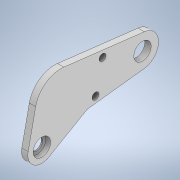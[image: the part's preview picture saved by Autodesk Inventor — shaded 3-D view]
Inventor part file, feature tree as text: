
AUTODESK INVENTOR PART (.ipt)
format: ipt  version: 2020 (Build 240168000, 168)  size: 390,656 bytes
history: native  units: mm
features: extrude x7, sketch x4, projected_geometry x3
ambient origin geometry x8: Origin, YZ Plane, XZ Plane, XY Plane, X Axis, Y Axis, Z Axis, Center Point
bodies: Body1 (feature_tree)
feature tree (14):
  extrude  "Выдавливание4"  Depth=18.6mm
  extrude  "Выдавливание5"  Depth=12.2mm
  extrude  "Выдавливание6"  Depth=9.7mm
  extrude  "Выдавливание7"  Depth=7.1mm
  sketch  "Эскиз7"
  extrude  "Выдавливание8"  Depth=38.82013mm
  extrude  "Выдавливание9"  Depth=38.8mm
  extrude  "Выдавливание10"  Depth=38.8mm
  sketch  "Эскиз4"
  projected_geometry  "Спроецированная петля3"
  sketch  "Эскиз5"
  sketch  "Эскиз6"
  projected_geometry  "Спроецированная петля4"
  projected_geometry  "Спроецированная петля5"
